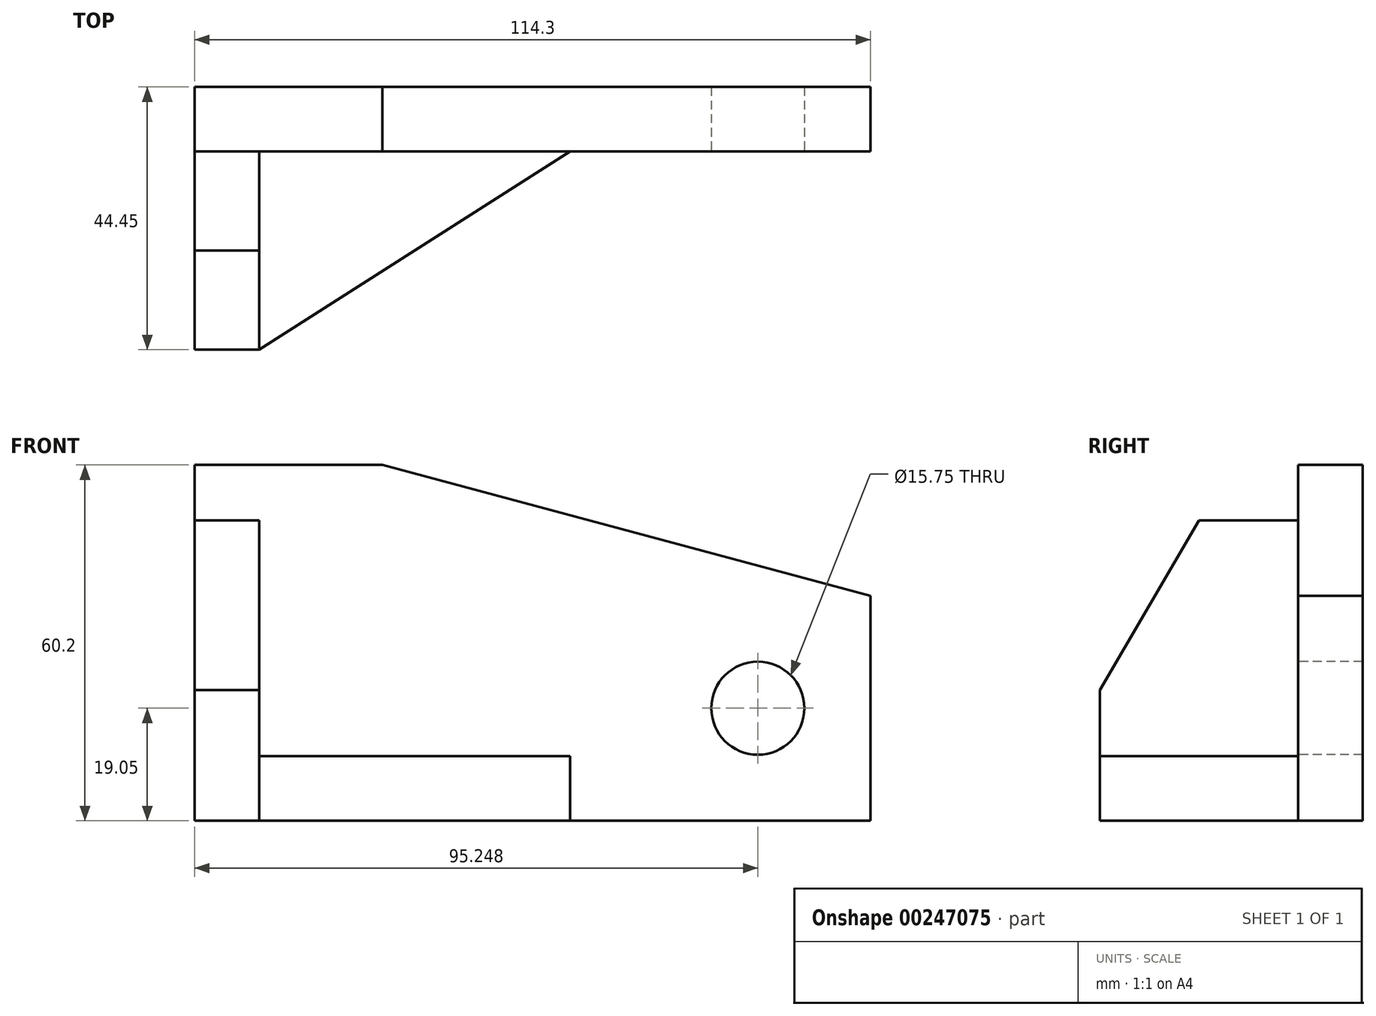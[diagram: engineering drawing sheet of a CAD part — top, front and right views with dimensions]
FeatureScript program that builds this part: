
annotation { "Feature Type Name" : "Feature", "Feature Type Description" : "" }
export const myFeature = defineFeature(function(context is Context, id is Id, definition is map)
    precondition{}
    {
        {
            var Q0;
            Q0=qCreatedBy(makeId("Top.planeOp"),FACE);
            var sketch = newSketch(context, id + "F0", { "sketchPlane" : qUnion([Q0])});
            skLineSegment(sketch, "E0", {"start": v(-75.97, 85.28) * mm, "end": v(38.33, 85.28) * mm});
            skLineSegment(sketch, "E1", {"start": v(38.33, 85.28) * mm, "end": v(38.33, 74.36) * mm});
            skLineSegment(sketch, "E2", {"start": v(-75.97, 85.28) * mm, "end": v(-75.97, 74.36) * mm});
            skLineSegment(sketch, "E3", {"start": v(-75.97, 74.36) * mm, "end": v(38.33, 74.36) * mm});
            skLineSegment(sketch, "E4", {"start": v(-75.97, 74.36) * mm, "end": v(-75.97, 40.83) * mm});
            skLineSegment(sketch, "E5", {"start": v(-75.97, 40.83) * mm, "end": v(-65.05, 40.83) * mm});
            skLineSegment(sketch, "E6", {"start": v(-65.05, 40.83) * mm, "end": v(-65.05, 74.36) * mm});
            skLineSegment(sketch, "E7", {"start": v(-65.05, 40.83) * mm, "end": v(-12.47, 74.36) * mm});
            skLineSegment(sketch, "E8", {"start": v(-44.22, 85.28) * mm, "end": v(-44.22, 74.36) * mm});
            skSolve(sketch);
        }
        {
            var Q0;
            {var subQ0=sQuery(id+"F0.wireOp",EDGE,"E6");Q0=makeQuery(id+"F0.imprint","IMPRINT",FACE,{"disambiguationData":[TD([[makeQuery(id+"F0.imprint","IMPRINT",EDGE,{"derivedFrom":subQ0}),-1.0]])]});}
            extrude(context, id + "F1", {"entities" : qUnion([Q0]), "depth" : 10.92 * mm});
        }
        {
            var Q0;
            {var subQ3=sQuery(id+"F0.wireOp",EDGE,"E2");Q0=makeQuery(id+"F0.imprint","IMPRINT",FACE,{"disambiguationData":[TD([[makeQuery(id+"F0.imprint","IMPRINT",EDGE,{"derivedFrom":subQ3}),1.0]])]});}
            var Q1;
            Q1=makeQuery(id+"F0.imprint","IMPRINT",FACE,{"disambiguationData":[TD([[makeQuery(id+"F0.imprint","IMPRINT",EDGE,{"derivedFrom":sQuery(id+"F0.wireOp",EDGE,"E0")}),-1.0]])]});
            extrude(context, id + "F2", {"entities" : qUnion([Q0, Q1]), "operationType" : NewBodyOperationType.ADD, "depth" : 60.2 * mm});
        }
        {
            var Q0;
            {var subQ0=sQuery(id+"F0.wireOp",EDGE,"E4");Q0=makeQuery(id+"F0.imprint","IMPRINT",FACE,{"disambiguationData":[TD([[makeQuery(id+"F0.imprint","IMPRINT",EDGE,{"derivedFrom":subQ0}),1.0]])]});}
            extrude(context, id + "F3", {"entities" : qUnion([Q0]), "operationType" : NewBodyOperationType.ADD, "depth" : 50.8 * mm});
        }
        {
            var Q0;
            Q0=makeQuery(id+"F3.opExtrude","SWEPT_FACE",FACE,{"disambiguationData":[OSD([sQuery(id+"F0.wireOp",EDGE,"E6")])]});
            var sketch = newSketch(context, id + "F4", { "sketchPlane" : qUnion([Q0])});
            skLineSegment(sketch, "E9", {"start": v(40.83, 50.8) * mm, "end": v(57.6, 50.8) * mm});
            skLineSegment(sketch, "E10", {"start": v(40.83, 22.1) * mm, "end": v(57.6, 50.8) * mm});
            skSolve(sketch);
        }
        {
            var Q0;
            {var subQ0=sQuery(id+"F4.wireOp",EDGE,"E9");Q0=makeQuery(id+"F4.imprint","IMPRINT",FACE,{"disambiguationData":[TD([[makeQuery(id+"F4.imprint","IMPRINT",EDGE,{"derivedFrom":subQ0}),-1.0]])]});}
            extrude(context, id + "F5", {"entities" : qUnion([Q0]), "operationType" : NewBodyOperationType.REMOVE, "oppositeDirection" : true, "depth" : 76.2 * mm});
        }
        {
            var Q0;
            Q0=makeQuery(id+"F2.opExtrude","SWEPT_FACE",FACE,{"disambiguationData":[OSD([sQuery(id+"F0.wireOp",EDGE,"E3")])]});
            var sketch = newSketch(context, id + "F6", { "sketchPlane" : qUnion([Q0])});
            skLineSegment(sketch, "E11", {"start": v(38.33, 60.2) * mm, "end": v(38.33, 38.08) * mm});
            skLineSegment(sketch, "E12", {"start": v(-44.22, 60.2) * mm, "end": v(38.33, 38.08) * mm});
            skCircle(sketch, "E13", {"center": v(19.28, 19.05) * mm, "radius": 7.87 * mm});
            skSolve(sketch);
        }
        {
            var Q0;
            {var subQ0=sQuery(id+"F6.wireOp",EDGE,"E11");Q0=makeQuery(id+"F6.imprint","IMPRINT",FACE,{"disambiguationData":[TD([[makeQuery(id+"F6.imprint","IMPRINT",EDGE,{"derivedFrom":subQ0}),-1.0]])]});}
            var Q1;
            Q1=makeQuery(id+"F6.imprint","IMPRINT",FACE,{"disambiguationData":[TD([[makeQuery(id+"F6.imprint","IMPRINT",EDGE,{"derivedFrom":sQuery(id+"F6.wireOp",EDGE,"E13")}),1.0]])]});
            extrude(context, id + "F7", {"entities" : qUnion([Q0, Q1]), "operationType" : NewBodyOperationType.REMOVE, "oppositeDirection" : true, "depth" : 76.2 * mm});
        }
    });
